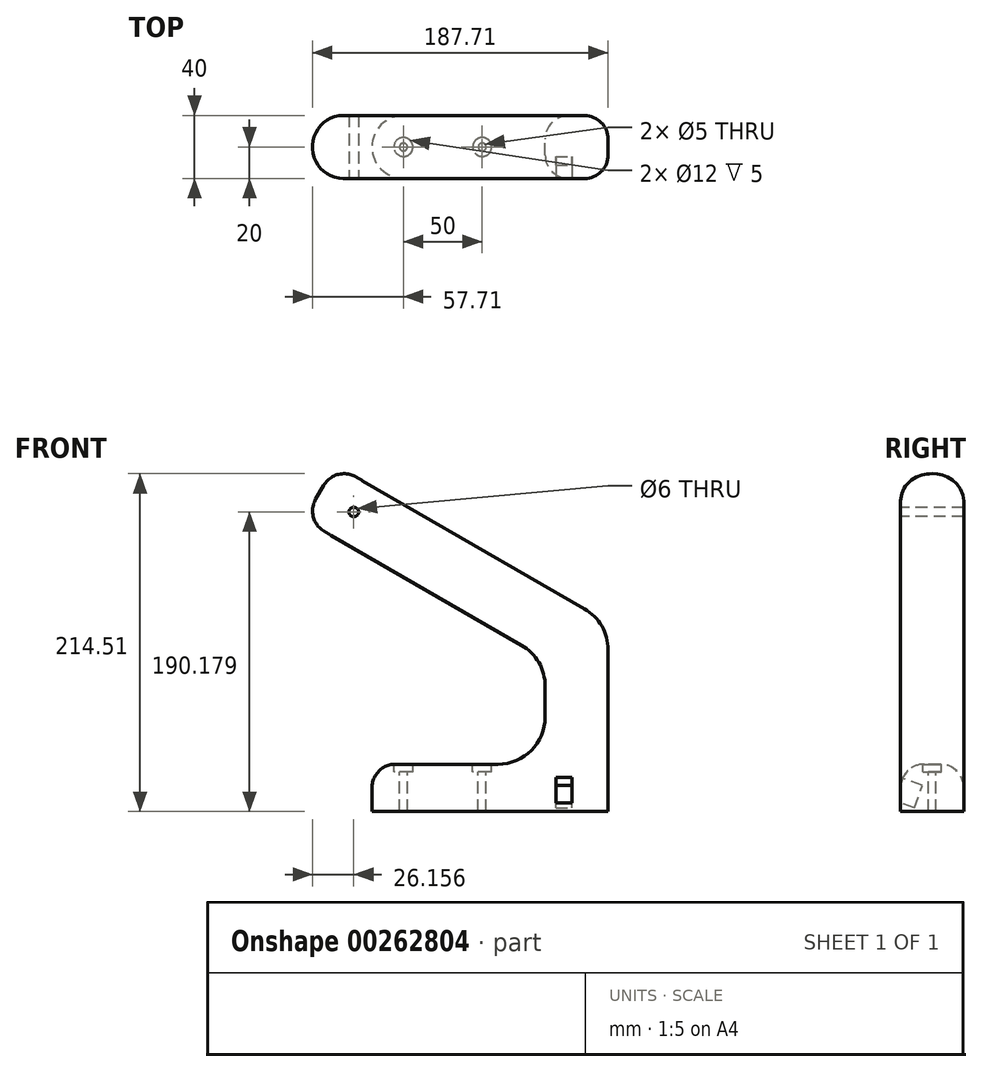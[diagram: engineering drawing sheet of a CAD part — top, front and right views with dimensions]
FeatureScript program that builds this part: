
annotation { "Feature Type Name" : "Feature", "Feature Type Description" : "" }
export const myFeature = defineFeature(function(context is Context, id is Id, definition is map)
    precondition{}
    {
        {
            var Q0;
            Q0=qCreatedBy(makeId("Front.planeOp"),FACE);
            var sketch = newSketch(context, id + "F0", { "sketchPlane" : qUnion([Q0])});
            skLineSegment(sketch, "E0", {"start": v(0, 0) * mm, "end": v(-150, 0) * mm});
            skLineSegment(sketch, "E1", {"start": v(-150, 0) * mm, "end": v(-150, 30) * mm});
            skLineSegment(sketch, "E2", {"start": v(-150, 30) * mm, "end": v(-40, 30) * mm});
            skLineSegment(sketch, "E3", {"start": v(-40, 30) * mm, "end": v(-40, 96.9) * mm});
            skLineSegment(sketch, "E4", {"start": v(-40, 96.9) * mm, "end": v(-193.2, 185.36) * mm});
            skLineSegment(sketch, "E5", {"start": v(0, 0) * mm, "end": v(0, 120) * mm});
            skLineSegment(sketch, "E6", {"start": v(0, 120) * mm, "end": v(-173.2, 220) * mm});
            skLineSegment(sketch, "E7", {"start": v(-193.2, 185.36) * mm, "end": v(-173.2, 220) * mm});
            skSolve(sketch);
        }
        {
            var Q0;
            Q0 = qSketchRegion(id + "F0", true);
            extrude(context, id + "F1", {"entities" : qUnion([Q0]), "depth" : 40 * mm, "symmetric" : true});
        }
        {
            var Q0;
            Q0=makeQuery(id+"F1.opExtrude","CAP_EDGE",EDGE,{"disambiguationData":[OSD([sQuery(id+"F0.wireOp",EDGE,"E7")])],"isStart":false});
            var Q1;
            Q1=makeQuery(id+"F1.opExtrude","CAP_EDGE",EDGE,{"disambiguationData":[OSD([sQuery(id+"F0.wireOp",EDGE,"E7")])],"isStart":true});
            var Q2;
            Q2=makeQuery(id+"F1.opExtrude","CAP_EDGE",EDGE,{"disambiguationData":[OSD([sQuery(id+"F0.wireOp",EDGE,"E1")])],"isStart":false});
            var Q3;
            Q3=makeQuery(id+"F1.opExtrude","CAP_EDGE",EDGE,{"disambiguationData":[OSD([sQuery(id+"F0.wireOp",EDGE,"E1")])],"isStart":true});
            fillet(context, id + "F2", {"entities" : qUnion([Q0, Q1, Q2, Q3]), "radius" : 20 * mm, "tangentPropagation" : true, "allowEdgeOverflow" : false});
        }
        {
            var Q0;
            Q0=makeQuery(id+"F1.opExtrude","SWEPT_EDGE",EDGE,{"disambiguationData":[OSD([sQuery(id+"F0.wireOp",EDGE,"E2"),sQuery(id+"F0.wireOp",EDGE,"E3")])]});
            var Q1;
            Q1=makeQuery(id+"F1.opExtrude","SWEPT_EDGE",EDGE,{"disambiguationData":[OSD([sQuery(id+"F0.wireOp",EDGE,"E3"),sQuery(id+"F0.wireOp",EDGE,"E4")])]});
            var Q2;
            Q2=makeQuery(id+"F1.opExtrude","SWEPT_EDGE",EDGE,{"disambiguationData":[OSD([sQuery(id+"F0.wireOp",EDGE,"E5"),sQuery(id+"F0.wireOp",EDGE,"E6")])]});
            fillet(context, id + "F3", {"entities" : qUnion([Q0, Q1, Q2]), "radius" : 30 * mm, "tangentPropagation" : true, "allowEdgeOverflow" : false});
        }
        {
            var Q0;
            Q0=makeQuery(id+"F1.opExtrude","SWEPT_FACE",FACE,{"disambiguationData":[OSD([sQuery(id+"F0.wireOp",EDGE,"E2")])]});
            var sketch = newSketch(context, id + "F4", { "sketchPlane" : qUnion([Q0])});
            skCircle(sketch, "E8", {"center": v(-130, 0) * mm, "radius": 2.5 * mm});
            skCircle(sketch, "E9", {"center": v(-80, 0) * mm, "radius": 2.5 * mm});
            skSolve(sketch);
        }
        {
            var Q0;
            Q0 = qSketchRegion(id + "F4", true);
            extrude(context, id + "F5", {"entities" : qUnion([Q0]), "operationType" : NewBodyOperationType.REMOVE, "endBound" : BoundingType.THROUGH_ALL, "oppositeDirection" : true, "depth" : 25 * mm});
        }
        {
            var Q0;
            Q0=makeQuery(id+"F1.opExtrude","SWEPT_FACE",FACE,{"disambiguationData":[OSD([sQuery(id+"F0.wireOp",EDGE,"E2")])]});
            var sketch = newSketch(context, id + "F6", { "sketchPlane" : qUnion([Q0])});
            skCircle(sketch, "E10", {"center": v(-130, 0) * mm, "radius": 6 * mm});
            skCircle(sketch, "E11", {"center": v(-80, 0) * mm, "radius": 6 * mm});
            skSolve(sketch);
        }
        {
            var Q0;
            Q0 = qSketchRegion(id + "F6", true);
            extrude(context, id + "F7", {"entities" : qUnion([Q0]), "operationType" : NewBodyOperationType.REMOVE, "oppositeDirection" : true, "depth" : 5 * mm});
        }
        {
            var Q0;
            Q0=makeQuery(id+"F1.opExtrude","CAP_EDGE",EDGE,{"disambiguationData":[OSD([sQuery(id+"F0.wireOp",EDGE,"E6")])],"isStart":false});
            var Q1;
            Q1=makeQuery(id+"F1.opExtrude","CAP_EDGE",EDGE,{"disambiguationData":[OSD([sQuery(id+"F0.wireOp",EDGE,"E4")])],"isStart":false});
            fillet(context, id + "F8", {"entities" : qUnion([Q0, Q1]), "radius" : 15 * mm, "tangentPropagation" : true, "allowEdgeOverflow" : false});
        }
        {
            var Q0;
            Q0=makeQuery(id+"F1.opExtrude","CAP_FACE",FACE,{"disambiguationData":[OSD([sQuery(id+"F0.wireOp",EDGE,"E0"),sQuery(id+"F0.wireOp",EDGE,"E1"),sQuery(id+"F0.wireOp",EDGE,"E2"),sQuery(id+"F0.wireOp",EDGE,"E3"),sQuery(id+"F0.wireOp",EDGE,"E4"),sQuery(id+"F0.wireOp",EDGE,"E5"),sQuery(id+"F0.wireOp",EDGE,"E6"),sQuery(id+"F0.wireOp",EDGE,"E7")])],"isStart":false});
            var sketch = newSketch(context, id + "F9", { "sketchPlane" : qUnion([Q0])});
            skCircle(sketch, "E12", {"center": v(-161.55, 190.18) * mm, "radius": 3 * mm});
            skSolve(sketch);
        }
        {
            var Q0;
            Q0 = qSketchRegion(id + "F9", true);
            extrude(context, id + "F10", {"entities" : qUnion([Q0]), "operationType" : NewBodyOperationType.REMOVE, "endBound" : BoundingType.THROUGH_ALL, "oppositeDirection" : true, "depth" : 25 * mm});
        }
        {
            var Q0;
            Q0=makeQuery(id+"F1.opExtrude","CAP_FACE",FACE,{"disambiguationData":[OSD([sQuery(id+"F0.wireOp",EDGE,"E0"),sQuery(id+"F0.wireOp",EDGE,"E1"),sQuery(id+"F0.wireOp",EDGE,"E2"),sQuery(id+"F0.wireOp",EDGE,"E3"),sQuery(id+"F0.wireOp",EDGE,"E4"),sQuery(id+"F0.wireOp",EDGE,"E5"),sQuery(id+"F0.wireOp",EDGE,"E6"),sQuery(id+"F0.wireOp",EDGE,"E7")])],"isStart":false});
            var Q1;
            {var subQ0=sQuery(id+"F0.wireOp",EDGE,"E2");Q1=makeQuery(id+"F8.opFillet","BLEND_EDGE",EDGE,{"blendedFrom":[makeQuery(id+"F1.opExtrude","CAP_EDGE",EDGE,{"disambiguationData":[OSD([subQ0])],"isStart":false}),makeQuery(id+"F1.opExtrude","CAP_FACE",FACE,{"disambiguationData":[OSD([sQuery(id+"F0.wireOp",EDGE,"E0"),sQuery(id+"F0.wireOp",EDGE,"E1"),subQ0,sQuery(id+"F0.wireOp",EDGE,"E3"),sQuery(id+"F0.wireOp",EDGE,"E4"),sQuery(id+"F0.wireOp",EDGE,"E5"),sQuery(id+"F0.wireOp",EDGE,"E6"),sQuery(id+"F0.wireOp",EDGE,"E7")])],"isStart":false})],"blendedInto":[makeQuery(id+"F1.opExtrude","CAP_FACE",FACE,{"disambiguationData":[OSD([sQuery(id+"F0.wireOp",EDGE,"E0"),sQuery(id+"F0.wireOp",EDGE,"E1"),subQ0,sQuery(id+"F0.wireOp",EDGE,"E3"),sQuery(id+"F0.wireOp",EDGE,"E4"),sQuery(id+"F0.wireOp",EDGE,"E5"),sQuery(id+"F0.wireOp",EDGE,"E6"),sQuery(id+"F0.wireOp",EDGE,"E7")])],"isStart":false})]});}
            cPlane(context, id + "F11", {"entities" : qUnion([Q0, Q1]), "cplaneType" : CPlaneType.LINE_ANGLE, "offset" : 25 * mm, "angle" : 20 * degree, "oppositeDirection" : true, "width" : 150 * mm, "height" : 150 * mm});
        }
        {
            var Q0;
            Q0=qCreatedBy(id+"F11.planeOp",FACE);
            var sketch = newSketch(context, id + "F12", { "sketchPlane" : qUnion([Q0])});
            skLineSegment(sketch, "E13.bottom", {"start": v(33.2, -1.84) * mm, "end": v(23, -1.84) * mm});
            skLineSegment(sketch, "E13.top", {"start": v(33.2, 13.36) * mm, "end": v(23, 13.36) * mm});
            skLineSegment(sketch, "E13.left", {"start": v(33.2, -1.84) * mm, "end": v(33.2, 13.36) * mm});
            skLineSegment(sketch, "E13.right", {"start": v(23, -1.84) * mm, "end": v(23, 13.36) * mm});
            skSolve(sketch);
        }
        {
            var Q0;
            Q0 = qSketchRegion(id + "F12", true);
            extrude(context, id + "F13", {"entities" : qUnion([Q0]), "operationType" : NewBodyOperationType.REMOVE, "depth" : 25 * mm, "symmetric" : true});
        }
    });
